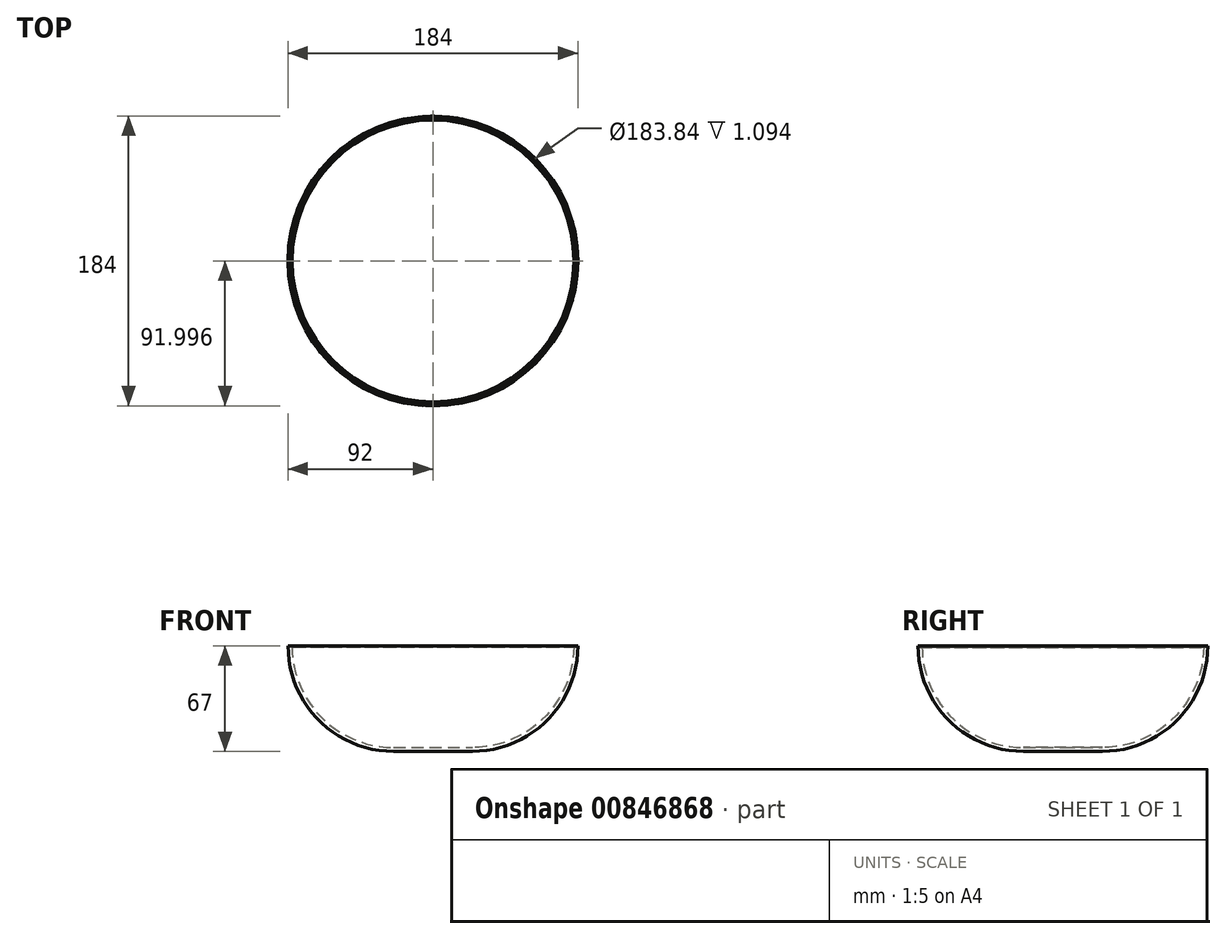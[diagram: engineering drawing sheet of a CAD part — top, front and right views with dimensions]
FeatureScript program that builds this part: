
annotation { "Feature Type Name" : "Feature", "Feature Type Description" : "" }
export const myFeature = defineFeature(function(context is Context, id is Id, definition is map)
    precondition{}
    {
        {
            var Q0;
            Q0=qCreatedBy(makeId("Right.planeOp"),FACE);
            var sketch = newSketch(context, id + "F0", { "sketchPlane" : qUnion([Q0])});
            skArc(sketch, "E0", {"start": v(-68.34, 52) * mm, "mid": v(-49.45, 6.4) * mm, "end": v(-3.84, -12.5) * mm});
            skLineSegment(sketch, "E1", {"start": v(-3.84, -12.5) * mm, "end": v(21.16, -12.5) * mm});
            skArc(sketch, "E2.0", {"start": v(-70.84, 52) * mm, "mid": v(-51.22, 4.62) * mm, "end": v(-3.84, -15) * mm});
            skLineSegment(sketch, "E3", {"start": v(-70.84, 52) * mm, "end": v(-68.34, 52) * mm});
            skLineSegment(sketch, "E4", {"start": v(-3.84, -15) * mm, "end": v(21.16, -15) * mm});
            skLineSegment(sketch, "E5", {"start": v(21.16, -15) * mm, "end": v(21.16, -12.5) * mm});
            skLineSegment(sketch, "E6", {"start": v(21.16, -15) * mm, "end": v(21.16, 14.91) * mm, "construction": true});
            skSolve(sketch);
        }
        {
            var Q0;
            Q0 = qSketchRegion(id + "F0", true);
            var Q1;
            Q1=sQuery(id+"F0.wireOp",EDGE,"E6");
            revolve(context, id + "F1", {"surfaceOperationType" : NewSurfaceOperationType.NEW, "entities" : qUnion([Q0]), "axis" : qUnion([Q1]), "revolveType" : RevolveType.FULL});
        }
        {
            var Q0;
            Q0=qCreatedBy(makeId("Right.planeOp"),FACE);
            var sketch = newSketch(context, id + "F2", { "sketchPlane" : qUnion([Q0])});
            skLineSegment(sketch, "E7", {"start": v(-70.76, 52) * mm, "end": v(-70.76, 50.9) * mm});
            skLineSegment(sketch, "E8", {"start": v(-70.76, 50.9) * mm, "end": v(-69.52, 50.9) * mm});
            skLineSegment(sketch, "E9", {"start": v(-69.52, 50.9) * mm, "end": v(-69.52, 52) * mm});
            skLineSegment(sketch, "E10", {"start": v(-69.52, 52) * mm, "end": v(-70.76, 52) * mm});
            skSolve(sketch);
        }
        {
            var Q0;
            Q0 = qSketchRegion(id + "F2", true);
            var Q1;
            Q1=sQuery(id+"F0.wireOp",EDGE,"E5");
            revolve(context, id + "F3", {"operationType" : NewBodyOperationType.REMOVE, "surfaceOperationType" : NewSurfaceOperationType.NEW, "entities" : qUnion([Q0]), "axis" : qUnion([Q1]), "revolveType" : RevolveType.FULL, "oppositeDirection" : true});
        }
    });
